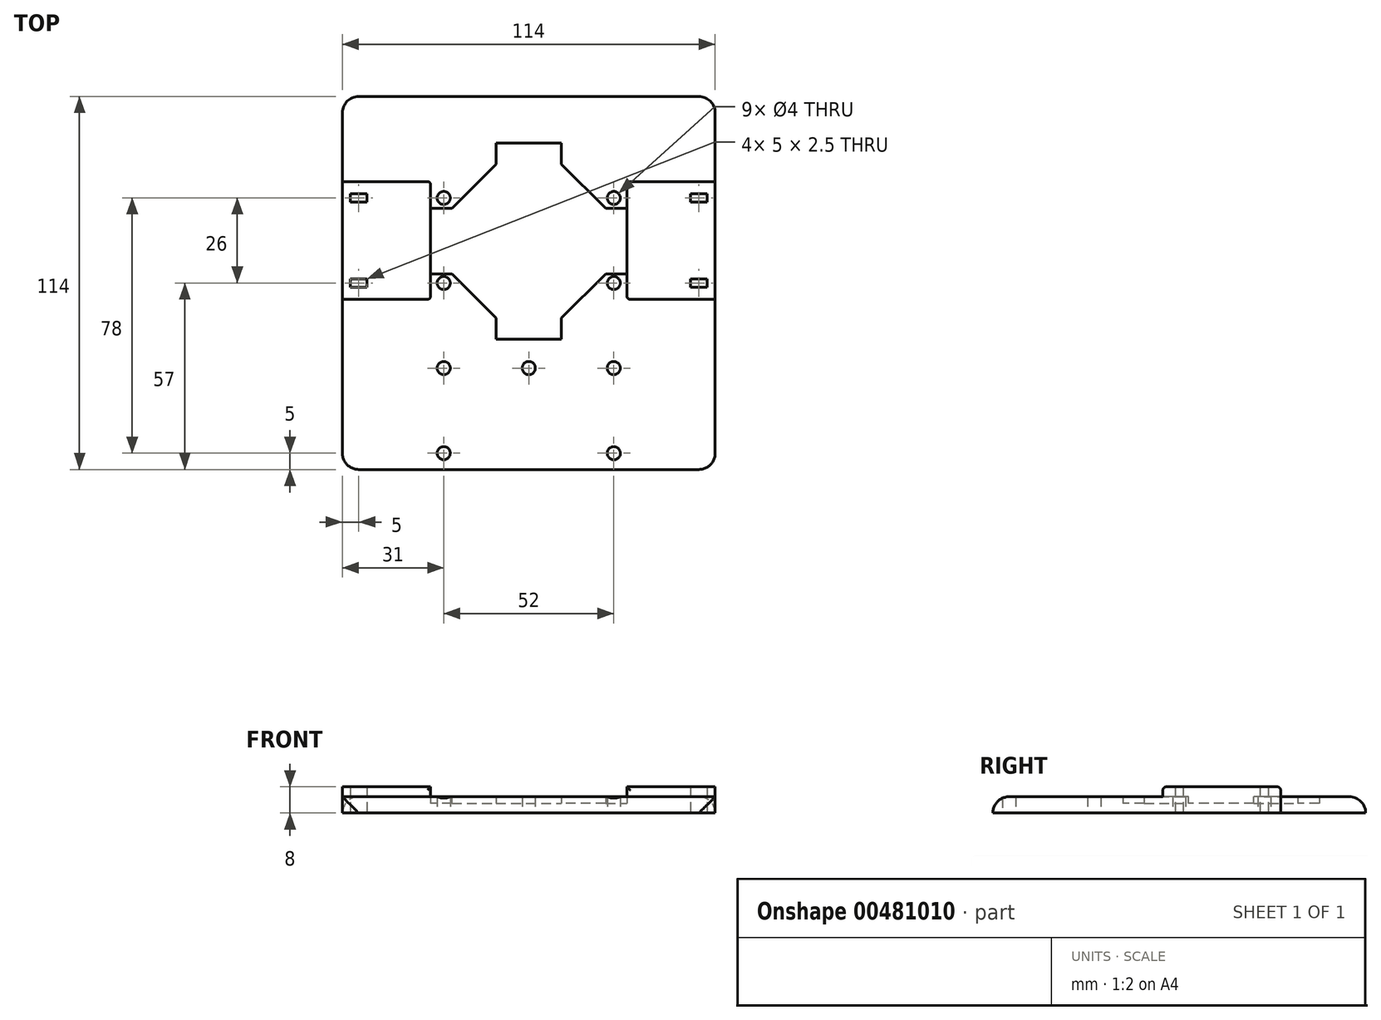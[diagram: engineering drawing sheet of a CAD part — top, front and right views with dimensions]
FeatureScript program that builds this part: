
annotation { "Feature Type Name" : "Feature", "Feature Type Description" : "" }
export const myFeature = defineFeature(function(context is Context, id is Id, definition is map)
    precondition{}
    {
        {
            var Q0;
            Q0=qCreatedBy(makeId("Top.planeOp"),FACE);
            var sketch = newSketch(context, id + "F0", { "sketchPlane" : qUnion([Q0])});
            skLineSegment(sketch, "E0.bottom", {"start": v(52, 52) * mm, "end": v(-52, 52) * mm, "construction": true});
            skLineSegment(sketch, "E0.top", {"start": v(52, -52) * mm, "end": v(-52, -52) * mm, "construction": true});
            skLineSegment(sketch, "E0.left", {"start": v(52, 52) * mm, "end": v(52, -52) * mm, "construction": true});
            skLineSegment(sketch, "E0.right", {"start": v(-52, 52) * mm, "end": v(-52, -52) * mm, "construction": true});
            skPoint(sketch, "E0.middle", {"position": v(0, 0) * mm});
            skPoint(sketch, "E1", {"position": v(-26, 52) * mm});
            skPoint(sketch, "E2", {"position": v(0, 52) * mm});
            skPoint(sketch, "E3", {"position": v(26, 52) * mm});
            skPoint(sketch, "E4", {"position": v(-52, 26) * mm});
            skPoint(sketch, "E5", {"position": v(-52, 0) * mm});
            skPoint(sketch, "E6", {"position": v(-52, -26) * mm});
            skLineSegment(sketch, "E7", {"start": v(-10, 22.8) * mm, "end": v(-30, 22.8) * mm});
            skLineSegment(sketch, "E8", {"start": v(-30, 22.8) * mm, "end": v(-30, 2.8) * mm});
            skLineSegment(sketch, "E9", {"start": v(-30, 2.8) * mm, "end": v(-10, 2.8) * mm});
            skLineSegment(sketch, "E10.1.0", {"start": v(-10, 2.8) * mm, "end": v(-10, -17.2) * mm});
            skLineSegment(sketch, "E10.1.1", {"start": v(-10, -17.2) * mm, "end": v(10, -17.2) * mm});
            skLineSegment(sketch, "E10.1.2", {"start": v(10, -17.2) * mm, "end": v(10, 2.8) * mm});
            skLineSegment(sketch, "E10.2.0", {"start": v(10, 2.8) * mm, "end": v(30, 2.8) * mm});
            skLineSegment(sketch, "E10.2.1", {"start": v(30, 2.8) * mm, "end": v(30, 22.8) * mm});
            skLineSegment(sketch, "E10.2.2", {"start": v(30, 22.8) * mm, "end": v(10, 22.8) * mm});
            skLineSegment(sketch, "E10.3.0", {"start": v(10, 22.8) * mm, "end": v(10, 42.8) * mm});
            skLineSegment(sketch, "E10.3.1", {"start": v(10, 42.8) * mm, "end": v(-10, 42.8) * mm});
            skLineSegment(sketch, "E10.3.2", {"start": v(-10, 42.8) * mm, "end": v(-10, 22.8) * mm});
            skPoint(sketch, "E10.center", {"position": v(0, 12.8) * mm});
            skLineSegment(sketch, "E11", {"start": v(-52, 26) * mm, "end": v(52, 26) * mm, "construction": true});
            skLineSegment(sketch, "E12", {"start": v(-52, 0) * mm, "end": v(52, 0) * mm, "construction": true});
            skLineSegment(sketch, "E13", {"start": v(-26, 52) * mm, "end": v(-26, -52) * mm, "construction": true});
            skLineSegment(sketch, "E14", {"start": v(26, 52) * mm, "end": v(26, -52) * mm, "construction": true});
            skLineSegment(sketch, "E15.bottom", {"start": v(57, 57) * mm, "end": v(-57, 57) * mm});
            skLineSegment(sketch, "E15.top", {"start": v(57, -57) * mm, "end": v(-57, -57) * mm});
            skLineSegment(sketch, "E15.left", {"start": v(57, 57) * mm, "end": v(57, -57) * mm});
            skLineSegment(sketch, "E15.right", {"start": v(-57, 57) * mm, "end": v(-57, -57) * mm});
            skLineSegment(sketch, "E16", {"start": v(0, 52) * mm, "end": v(0, -52) * mm, "construction": true});
            skLineSegment(sketch, "E17.bottom", {"start": v(-57, 31) * mm, "end": v(-30, 31) * mm});
            skLineSegment(sketch, "E17.top", {"start": v(-57, -5) * mm, "end": v(-30, -5) * mm});
            skLineSegment(sketch, "E17.left", {"start": v(-57, 31) * mm, "end": v(-57, -5) * mm});
            skLineSegment(sketch, "E17.right", {"start": v(-30, 31) * mm, "end": v(-30, -5) * mm});
            skLineSegment(sketch, "E18.MirrorCS", {"start": v(57, -5) * mm, "end": v(30, -5) * mm});
            skLineSegment(sketch, "E19.MirrorCS", {"start": v(30, 31) * mm, "end": v(30, -5) * mm});
            skLineSegment(sketch, "E20.MirrorCS", {"start": v(57, 31) * mm, "end": v(30, 31) * mm});
            skLineSegment(sketch, "E21.MirrorCS", {"start": v(30, 22.8) * mm, "end": v(30, 2.8) * mm});
            skPoint(sketch, "E22", {"position": v(-26, 26) * mm});
            skPoint(sketch, "E23", {"position": v(26, 26) * mm});
            skPoint(sketch, "E24", {"position": v(26, 0) * mm});
            skPoint(sketch, "E25", {"position": v(-26, 0) * mm});
            skLineSegment(sketch, "E26.bottom", {"start": v(-49.5, 27.25) * mm, "end": v(-54.5, 27.25) * mm});
            skLineSegment(sketch, "E26.top", {"start": v(-49.5, 24.75) * mm, "end": v(-54.5, 24.75) * mm});
            skLineSegment(sketch, "E26.left", {"start": v(-49.5, 27.25) * mm, "end": v(-49.5, 24.75) * mm});
            skLineSegment(sketch, "E26.right", {"start": v(-54.5, 27.25) * mm, "end": v(-54.5, 24.75) * mm});
            skLineSegment(sketch, "E27.MirrorCS", {"start": v(49.5, 24.75) * mm, "end": v(54.5, 24.75) * mm});
            skLineSegment(sketch, "E28.MirrorCS", {"start": v(49.5, 27.25) * mm, "end": v(54.5, 27.25) * mm});
            skLineSegment(sketch, "E29.MirrorCS", {"start": v(54.5, 27.25) * mm, "end": v(54.5, 24.75) * mm});
            skLineSegment(sketch, "E30.MirrorCS", {"start": v(49.5, 27.25) * mm, "end": v(49.5, 24.75) * mm});
            skLineSegment(sketch, "E31", {"start": v(-30, 13) * mm, "end": v(30, 13) * mm, "construction": true});
            skLineSegment(sketch, "E32.MirrorCS", {"start": v(-49.5, -1.25) * mm, "end": v(-49.5, 1.25) * mm});
            skLineSegment(sketch, "E33.MirrorCS", {"start": v(-49.5, -1.25) * mm, "end": v(-54.5, -1.25) * mm});
            skLineSegment(sketch, "E34.MirrorCS", {"start": v(-49.5, 1.25) * mm, "end": v(-54.5, 1.25) * mm});
            skLineSegment(sketch, "E35.MirrorCS", {"start": v(-54.5, -1.25) * mm, "end": v(-54.5, 1.25) * mm});
            skLineSegment(sketch, "E36.MirrorCS", {"start": v(54.5, -1.25) * mm, "end": v(54.5, 1.25) * mm});
            skLineSegment(sketch, "E37.MirrorCS", {"start": v(49.5, -1.25) * mm, "end": v(54.5, -1.25) * mm});
            skLineSegment(sketch, "E38.MirrorCS", {"start": v(49.5, -1.25) * mm, "end": v(49.5, 1.25) * mm});
            skLineSegment(sketch, "E39.MirrorCS", {"start": v(49.5, 1.25) * mm, "end": v(54.5, 1.25) * mm});
            skPoint(sketch, "E40", {"position": v(0, 13) * mm});
            skLineSegment(sketch, "E41", {"start": v(-52, -26) * mm, "end": v(52, -26) * mm, "construction": true});
            skPoint(sketch, "E42", {"position": v(-26, -26) * mm});
            skPoint(sketch, "E43", {"position": v(26, -26) * mm});
            skPoint(sketch, "E44", {"position": v(0, -26) * mm});
            skSolve(sketch);
        }
        {
            var Q0;
            {var subQ0=sQuery(id+"F0.wireOp",EDGE,"E7");Q0=makeQuery(id+"F0.imprint","IMPRINT",FACE,{"disambiguationData":[TD([[makeQuery(id+"F0.imprint","IMPRINT",EDGE,{"derivedFrom":subQ0}),1.0]])]});}
            extrude(context, id + "F1", {"entities" : qUnion([Q0]), "depth" : 3 * mm});
        }
        {
            var Q0;
            {var subQ6=sQuery(id+"F0.wireOp",EDGE,"E7");Q0=makeQuery(id+"F0.imprint","IMPRINT",FACE,{"disambiguationData":[TD([[makeQuery(id+"F0.imprint","IMPRINT",EDGE,{"derivedFrom":subQ6}),-1.0]])]});}
            var Q1;
            {var subQ2=sQuery(id+"F0.wireOp",EDGE,"E9");Q1=makeQuery(id+"F0.imprint","IMPRINT",FACE,{"disambiguationData":[TD([[makeQuery(id+"F0.imprint","IMPRINT",EDGE,{"derivedFrom":subQ2}),-1.0]])]});}
            extrude(context, id + "F2", {"entities" : qUnion([Q0, Q1]), "operationType" : NewBodyOperationType.ADD, "depth" : 5 * mm});
        }
        {
            var Q0;
            {var subQ4=sQuery(id+"F0.wireOp",EDGE,"E17.bottom");Q0=makeQuery(id+"F0.imprint","IMPRINT",FACE,{"disambiguationData":[TD([[makeQuery(id+"F0.imprint","IMPRINT",EDGE,{"derivedFrom":subQ4}),-1.0]])]});}
            var Q1;
            {var subQ2=sQuery(id+"F0.wireOp",EDGE,"E18.MirrorCS");Q1=makeQuery(id+"F0.imprint","IMPRINT",FACE,{"disambiguationData":[TD([[makeQuery(id+"F0.imprint","IMPRINT",EDGE,{"derivedFrom":subQ2}),-1.0]])]});}
            extrude(context, id + "F3", {"entities" : qUnion([Q0, Q1]), "operationType" : NewBodyOperationType.ADD, "depth" : 8 * mm});
        }
        {
            var Q0;
            Q0=sQuery(id+"F0.wireOp",VERTEX,"E22");
            var Q1;
            Q1=sQuery(id+"F0.wireOp",VERTEX,"E23");
            var Q2;
            Q2=sQuery(id+"F0.wireOp",VERTEX,"E24");
            var Q3;
            Q3=sQuery(id+"F0.wireOp",VERTEX,"E25");
            var Q4;
            Q4=sQuery(id+"F0.wireOp",VERTEX,"E13.end");
            var Q5;
            Q5=sQuery(id+"F0.wireOp",VERTEX,"E14.end");
            var Q6;
            Q6=sQuery(id+"F0.wireOp",VERTEX,"E42");
            var Q7;
            Q7=sQuery(id+"F0.wireOp",VERTEX,"E44");
            var Q8;
            Q8=sQuery(id+"F0.wireOp",VERTEX,"E43");
            var Q9;
            Q9=makeQuery(id+"F1.opExtrude","SWEPT_BODY",BODY,{"disambiguationData":[OSD([sQuery(id+"F0.wireOp",EDGE,"E7"),sQuery(id+"F0.wireOp",EDGE,"E9"),sQuery(id+"F0.wireOp",EDGE,"E10.1.0"),sQuery(id+"F0.wireOp",EDGE,"E10.1.1"),sQuery(id+"F0.wireOp",EDGE,"E10.1.2"),sQuery(id+"F0.wireOp",EDGE,"E10.2.0"),sQuery(id+"F0.wireOp",EDGE,"E10.2.2"),sQuery(id+"F0.wireOp",EDGE,"E10.3.0"),sQuery(id+"F0.wireOp",EDGE,"E10.3.1"),sQuery(id+"F0.wireOp",EDGE,"E10.3.2"),sQuery(id+"F0.wireOp",EDGE,"E17.right"),sQuery(id+"F0.wireOp",EDGE,"E21.MirrorCS")])]});
            hole(context, id + "F4", {"style" : HoleStyle.SIMPLE, "endStyle" : HoleEndStyle.THROUGH, "oppositeDirection" : true, "holeDiameter" : 4 * mm, "isTappedThrough" : true, "tappedDepth" : 12 * mm, "tapClearance" : 3, "locations" : qUnion([Q0, Q1, Q2, Q3, Q4, Q5, Q6, Q7, Q8]), "scope" : qUnion([Q9])});
        }
        {
            var Q0;
            Q0=makeQuery(id+"F2.opExtrude","SWEPT_EDGE",EDGE,{"disambiguationData":[OSD([sQuery(id+"F0.wireOp",EDGE,"E10.2.2"),sQuery(id+"F0.wireOp",EDGE,"E10.3.0")])]});
            var Q1;
            Q1=makeQuery(id+"F2.opExtrude","SWEPT_EDGE",EDGE,{"disambiguationData":[OSD([sQuery(id+"F0.wireOp",EDGE,"E10.1.2"),sQuery(id+"F0.wireOp",EDGE,"E10.2.0")])]});
            var Q2;
            Q2=makeQuery(id+"F2.opExtrude","SWEPT_EDGE",EDGE,{"disambiguationData":[OSD([sQuery(id+"F0.wireOp",EDGE,"E9"),sQuery(id+"F0.wireOp",EDGE,"E10.1.0")])]});
            var Q3;
            Q3=makeQuery(id+"F2.opExtrude","SWEPT_EDGE",EDGE,{"disambiguationData":[OSD([sQuery(id+"F0.wireOp",EDGE,"E7"),sQuery(id+"F0.wireOp",EDGE,"E10.3.2")])]});
            chamfer(context, id + "F5", {"entities" : qUnion([Q0, Q1, Q2, Q3]), "width" : 13.5 * mm, "tangentPropagation" : true});
        }
        {
            var Q0;
            Q0=makeQuery(id+"F2.opExtrude","CAP_EDGE",EDGE,{"disambiguationData":[OSD([sQuery(id+"F0.wireOp",EDGE,"E17.top")])],"isStart":false});
            var Q1;
            Q1=makeQuery(id+"F3.opExtrude","CAP_EDGE",EDGE,{"disambiguationData":[OSD([sQuery(id+"F0.wireOp",EDGE,"E17.top")])],"isStart":false});
            var Q2;
            Q2=makeQuery(id+"F3.opExtrude","SWEPT_EDGE",EDGE,{"disambiguationData":[OSD([sQuery(id+"F0.wireOp",EDGE,"E17.top"),sQuery(id+"F0.wireOp",EDGE,"E17.right")])]});
            var Q3;
            Q3=makeQuery(id+"F3.opExtrude","SWEPT_EDGE",EDGE,{"disambiguationData":[OSD([sQuery(id+"F0.wireOp",EDGE,"E17.bottom"),sQuery(id+"F0.wireOp",EDGE,"E17.right")])]});
            var Q4;
            Q4=makeQuery(id+"F2.opExtrude","CAP_EDGE",EDGE,{"disambiguationData":[OSD([sQuery(id+"F0.wireOp",EDGE,"E17.bottom")])],"isStart":false});
            var Q5;
            Q5=makeQuery(id+"F3.opExtrude","CAP_EDGE",EDGE,{"disambiguationData":[OSD([sQuery(id+"F0.wireOp",EDGE,"E17.bottom")])],"isStart":false});
            var Q6;
            Q6=makeQuery(id+"F2.opExtrude","CAP_EDGE",EDGE,{"disambiguationData":[OSD([sQuery(id+"F0.wireOp",EDGE,"E18.MirrorCS")])],"isStart":false});
            var Q7;
            Q7=makeQuery(id+"F3.opExtrude","CAP_EDGE",EDGE,{"disambiguationData":[OSD([sQuery(id+"F0.wireOp",EDGE,"E18.MirrorCS")])],"isStart":false});
            var Q8;
            Q8=makeQuery(id+"F3.opExtrude","SWEPT_EDGE",EDGE,{"disambiguationData":[OSD([sQuery(id+"F0.wireOp",EDGE,"E18.MirrorCS"),sQuery(id+"F0.wireOp",EDGE,"E19.MirrorCS")])]});
            var Q9;
            Q9=makeQuery(id+"F3.opExtrude","CAP_EDGE",EDGE,{"disambiguationData":[OSD([sQuery(id+"F0.wireOp",EDGE,"E20.MirrorCS")])],"isStart":false});
            var Q10;
            Q10=makeQuery(id+"F2.opExtrude","CAP_EDGE",EDGE,{"disambiguationData":[OSD([sQuery(id+"F0.wireOp",EDGE,"E20.MirrorCS")])],"isStart":false});
            var Q11;
            Q11=makeQuery(id+"F3.opExtrude","SWEPT_EDGE",EDGE,{"disambiguationData":[OSD([sQuery(id+"F0.wireOp",EDGE,"E19.MirrorCS"),sQuery(id+"F0.wireOp",EDGE,"E20.MirrorCS")])]});
            fillet(context, id + "F6", {"entities" : qUnion([Q0, Q1, Q2, Q3, Q4, Q5, Q6, Q7, Q8, Q9, Q10, Q11]), "radius" : 1 * mm, "tangentPropagation" : true, "allowEdgeOverflow" : false});
        }
        {
            var Q0;
            Q0=makeQuery(id+"F2.opExtrude","CAP_EDGE",EDGE,{"disambiguationData":[OSD([sQuery(id+"F0.wireOp",EDGE,"E15.bottom")])],"isStart":false});
            var Q1;
            Q1=makeQuery(id+"F2.opExtrude","SWEPT_EDGE",EDGE,{"disambiguationData":[OSD([sQuery(id+"F0.wireOp",EDGE,"E15.bottom"),sQuery(id+"F0.wireOp",EDGE,"E15.right")])]});
            var Q2;
            {var subQ0=sQuery(id+"F0.wireOp",EDGE,"E15.right");Q2=makeQuery(id+"F2.opExtrude","CAP_EDGE",EDGE,{"disambiguationData":[OSD([subQ0]),TDD([makeQuery(id+"F0.imprint","IMPRINT",EDGE,{"disambiguationData":[TD([[makeQuery(id+"F0.imprint","INTERSECT",VERTEX,{"derivedFrom":[sQuery(id+"F0.wireOp",EDGE,"E15.bottom"),subQ0]}),-1.0]])],"derivedFrom":subQ0})])],"isStart":false});}
            var Q3;
            Q3=makeQuery(id+"F2.opExtrude","SWEPT_EDGE",EDGE,{"disambiguationData":[OSD([sQuery(id+"F0.wireOp",EDGE,"E15.bottom"),sQuery(id+"F0.wireOp",EDGE,"E15.left")])]});
            var Q4;
            {var subQ0=sQuery(id+"F0.wireOp",EDGE,"E15.left");Q4=makeQuery(id+"F2.opExtrude","CAP_EDGE",EDGE,{"disambiguationData":[OSD([subQ0]),TDD([makeQuery(id+"F0.imprint","IMPRINT",EDGE,{"disambiguationData":[TD([[makeQuery(id+"F0.imprint","INTERSECT",VERTEX,{"derivedFrom":[sQuery(id+"F0.wireOp",EDGE,"E15.bottom"),subQ0]}),-1.0]])],"derivedFrom":subQ0})])],"isStart":false});}
            var Q5;
            Q5=makeQuery(id+"F2.opExtrude","CAP_EDGE",EDGE,{"disambiguationData":[OSD([sQuery(id+"F0.wireOp",EDGE,"E15.top")])],"isStart":false});
            var Q6;
            Q6=makeQuery(id+"F2.opExtrude","SWEPT_EDGE",EDGE,{"disambiguationData":[OSD([sQuery(id+"F0.wireOp",EDGE,"E15.top"),sQuery(id+"F0.wireOp",EDGE,"E15.right")])]});
            var Q7;
            Q7=makeQuery(id+"F2.opExtrude","SWEPT_EDGE",EDGE,{"disambiguationData":[OSD([sQuery(id+"F0.wireOp",EDGE,"E15.top"),sQuery(id+"F0.wireOp",EDGE,"E15.left")])]});
            fillet(context, id + "F7", {"entities" : qUnion([Q0, Q1, Q2, Q3, Q4, Q5, Q6, Q7]), "radius" : 5 * mm, "tangentPropagation" : true, "allowEdgeOverflow" : false});
        }
    });
